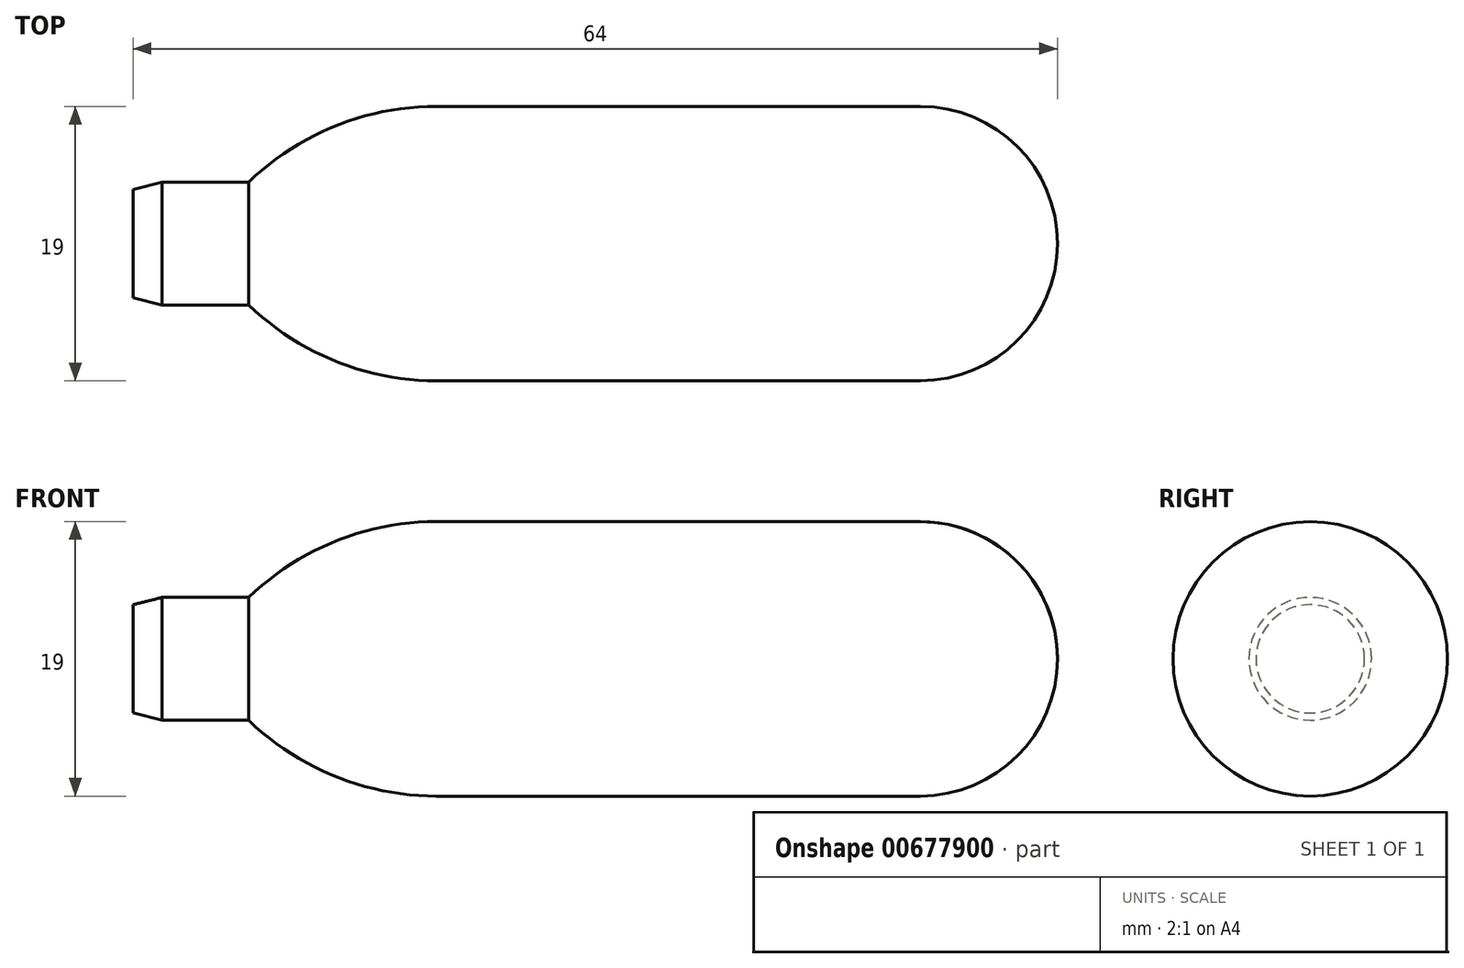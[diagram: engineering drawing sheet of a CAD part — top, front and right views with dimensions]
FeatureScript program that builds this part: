
annotation { "Feature Type Name" : "Feature", "Feature Type Description" : "" }
export const myFeature = defineFeature(function(context is Context, id is Id, definition is map)
    precondition{}
    {
        {
            var Q0;
            Q0=qCreatedBy(makeId("Front.planeOp"),FACE);
            var sketch = newSketch(context, id + "F0", { "sketchPlane" : qUnion([Q0])});
            skLineSegment(sketch, "E0", {"start": v(0, 0) * mm, "end": v(64, 0) * mm});
            skArc(sketch, "E1", {"start": v(64, 0) * mm, "mid": v(61.22, 6.72) * mm, "end": v(54.5, 9.5) * mm});
            skLineSegment(sketch, "E2", {"start": v(0, 0) * mm, "end": v(0, 3.75) * mm});
            skLineSegment(sketch, "E3", {"start": v(0, 3.75) * mm, "end": v(2, 4.25) * mm});
            skLineSegment(sketch, "E4", {"start": v(2, 4.25) * mm, "end": v(8, 4.25) * mm});
            skLineSegment(sketch, "E5", {"start": v(54.5, 9.5) * mm, "end": v(21, 9.5) * mm});
            skArc(sketch, "E6", {"start": v(21, 9.5) * mm, "mid": v(13.99, 8.14) * mm, "end": v(8, 4.25) * mm});
            skSolve(sketch);
        }
        {
            var Q0;
            Q0=makeQuery(id+"F0.imprint","IMPRINT",FACE,{"disambiguationData":[TD([[makeQuery(id+"F0.imprint","IMPRINT",EDGE,{"derivedFrom":sQuery(id+"F0.wireOp",EDGE,"E0")}),1.0]])]});
            var Q1;
            Q1=sQuery(id+"F0.wireOp",EDGE,"E0");
            revolve(context, id + "F1", {"entities" : qUnion([Q0]), "axis" : qUnion([Q1]), "revolveType" : RevolveType.FULL});
        }
    });
